# Revit family: Gelenkbogen-Element_vertikal_Russia
name_source: partatom
category: Generic Models
revit_build: Autodesk Revit 2015 (Build: 20140606_1530(x64)
units: mm (PartAtom-declared; Revit-internal decimal feet)

## types (7) — shared parameters
Manufacturer = OBO Bettermann
Material = Steel, Galvanized
URL = http://www.obo-bettermann.com

## per-type parameters (varying)
| type | B | GTIN | Manufacturer Art. No. |
| RGBEV 610 FS RU | 100 mm  [stored 0.328084 ft] | 4012196606238 | 7005431 |
| RGBEV 615 FS RU | 150 mm | 4012196649426 | 7005432 |
| RGBEV 620 FS RU | 200 mm  [stored 0.656168 ft] | 4012196606245 | 7005433 |
| RGBEV 630 FS RU | 300 mm | 4012196606252 | 7005435 |
| RGBEV 640 FS RU | 400 mm  [stored 1.31234 ft] | 4012196626328 | 7005437 |
| RGBEV 650 FS RU | 500 mm  [stored 1.64042 ft] | 4012196626335 | 7005439 |
| RGBEV 660 FS RU | 600 mm | 4012196626342 | 7005441 |

note: column(s) folded — value = type name in every type: Article Type

note: [stored X ft] marks values corroborated as IEEE doubles in the binary element streams (Revit-internal decimal feet)

## geometry (parser evidence)
native form markers: Sweep x2
no freeform markers — native parametric forms only
